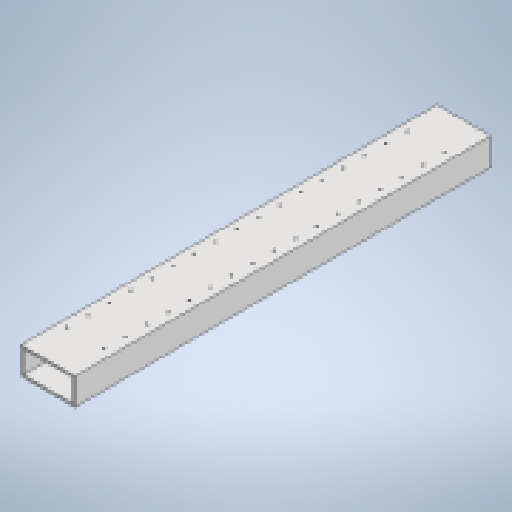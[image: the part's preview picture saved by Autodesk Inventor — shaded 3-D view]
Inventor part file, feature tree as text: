
AUTODESK INVENTOR PART (.ipt)
format: ipt  version: 2023 (Build 270158000, 158)  size: 182,784 bytes
history: native  units: in
note: dims shown in document units (in); Inventor stores cm internally (conversion verified against a paired STEP export)
features: other x4, extrude x2, sketch x2, reference x2, shell x1
ambient origin geometry x8: Origin, YZ Plane, XZ Plane, XY Plane, X Axis, Y Axis, Z Axis, Center Point
bodies: Solid1 (feature_tree)
feature tree (11):
  extrude  "Extrusion1"  Depth=3.0in
  shell  "Shell1"  Thickness=46.232in
  extrude  "Extrusion2"  Depth=46.232in TaperAngle=0.0deg
  sketch  "Sketch1"  dims[d0=6.0in d1=3.0in d2=46.232in d3=0.0in]
  sketch  "Sketch2"  dims[d4=0.25in d5=46.232in d6=0.0in]
  reference  "Reference1"
  reference  "Reference2"
  other  "<userpath>\Desktop\CNC_Project\FrameV2.iam"
  other  "FrameV2.iam"
  other  "HGW20CC_Rail_800mm:4"
  other  "HGW20CC_Rail_800mm:3"
